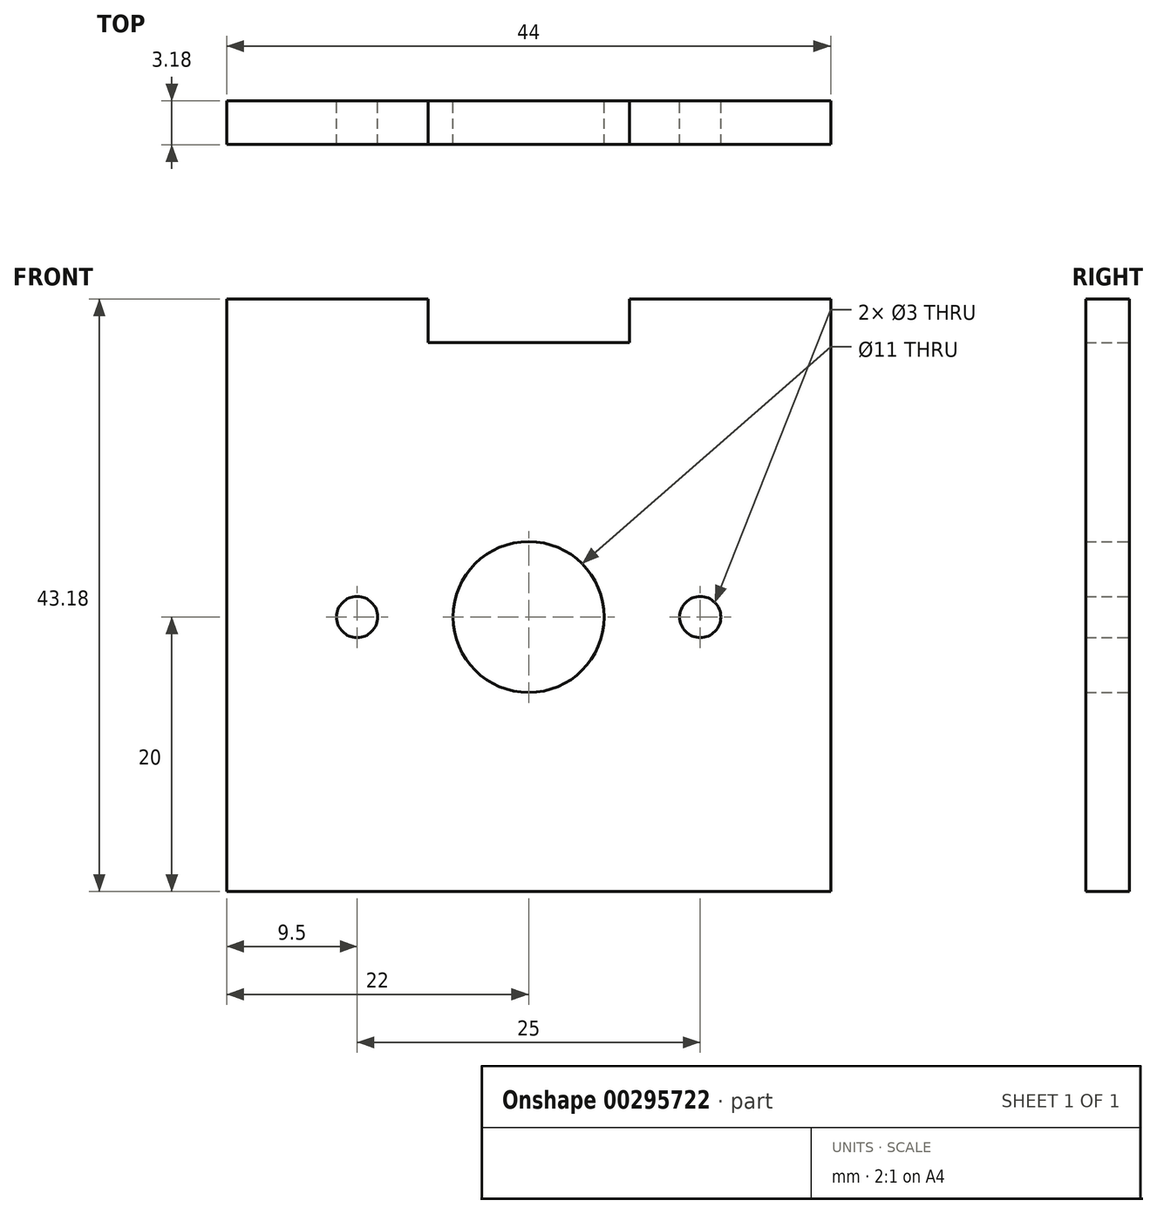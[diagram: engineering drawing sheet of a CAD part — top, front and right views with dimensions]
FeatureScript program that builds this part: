
annotation { "Feature Type Name" : "Feature", "Feature Type Description" : "" }
export const myFeature = defineFeature(function(context is Context, id is Id, definition is map)
    precondition{}
    {
        {
            var Q0;
            Q0=qCreatedBy(makeId("Front.planeOp"),FACE);
            var sketch = newSketch(context, id + "F0", { "sketchPlane" : qUnion([Q0])});
            skCircle(sketch, "E0", {"center": v(0, 0) * mm, "radius": 5.5 * mm});
            skCircle(sketch, "E1", {"center": v(12.5, 0) * mm, "radius": 1.5 * mm});
            skCircle(sketch, "E2.MirrorC", {"center": v(-12.5, 0) * mm, "radius": 1.5 * mm});
            skLineSegment(sketch, "E3.bottom", {"start": v(22, -20) * mm, "end": v(-22, -20) * mm});
            skLineSegment(sketch, "E3.top", {"start": v(22, 20) * mm, "end": v(-22, 20) * mm});
            skLineSegment(sketch, "E3.left", {"start": v(22, -20) * mm, "end": v(22, 20) * mm});
            skLineSegment(sketch, "E3.right", {"start": v(-22, -20) * mm, "end": v(-22, 20) * mm});
            skSolve(sketch);
        }
        {
            var Q0;
            Q0 = qSketchRegion(id + "F0", true);
            extrude(context, id + "F1", {"entities" : qUnion([Q0]), "depth" : 3.17 * mm});
        }
        {
            var Q0;
            Q0=makeQuery(id+"F1.opExtrude","SWEPT_FACE",FACE,{"disambiguationData":[OSD([sQuery(id+"F0.wireOp",EDGE,"E3.top")])]});
            var sketch = newSketch(context, id + "F2", { "sketchPlane" : qUnion([Q0])});
            skLineSegment(sketch, "E4.bottom", {"start": v(-22, 0) * mm, "end": v(-7.33, 0) * mm});
            skLineSegment(sketch, "E4.top", {"start": v(-22, -3.18) * mm, "end": v(-7.33, -3.18) * mm});
            skLineSegment(sketch, "E4.left", {"start": v(-22, 0) * mm, "end": v(-22, -3.18) * mm});
            skLineSegment(sketch, "E4.right", {"start": v(-7.33, 0) * mm, "end": v(-7.33, -3.18) * mm});
            skLineSegment(sketch, "E5.bottom", {"start": v(-7.33, -3.18) * mm, "end": v(7.33, -3.18) * mm});
            skLineSegment(sketch, "E5.top", {"start": v(-7.33, 0) * mm, "end": v(7.33, 0) * mm});
            skLineSegment(sketch, "E5.left", {"start": v(-7.33, -3.18) * mm, "end": v(-7.33, 0) * mm});
            skLineSegment(sketch, "E5.right", {"start": v(7.33, -3.18) * mm, "end": v(7.33, 0) * mm});
            skLineSegment(sketch, "E6.bottom", {"start": v(7.33, 0) * mm, "end": v(22, 0) * mm});
            skLineSegment(sketch, "E6.top", {"start": v(7.33, -3.18) * mm, "end": v(22, -3.18) * mm});
            skLineSegment(sketch, "E6.left", {"start": v(7.33, 0) * mm, "end": v(7.33, -3.18) * mm});
            skLineSegment(sketch, "E6.right", {"start": v(22, 0) * mm, "end": v(22, -3.18) * mm});
            skSolve(sketch);
        }
        {
            var Q0;
            Q0=makeQuery(id+"F2.imprint","IMPRINT",FACE,{"disambiguationData":[TD([[makeQuery(id+"F2.imprint","IMPRINT",EDGE,{"derivedFrom":sQuery(id+"F2.wireOp",EDGE,"E4.bottom")}),1.0]])]});
            var Q1;
            Q1=makeQuery(id+"F2.imprint","IMPRINT",FACE,{"disambiguationData":[TD([[makeQuery(id+"F2.imprint","IMPRINT",EDGE,{"derivedFrom":sQuery(id+"F2.wireOp",EDGE,"E6.bottom")}),1.0]])]});
            extrude(context, id + "F3", {"entities" : qUnion([Q0, Q1]), "operationType" : NewBodyOperationType.ADD, "depth" : 3.17 * mm});
        }
    });
